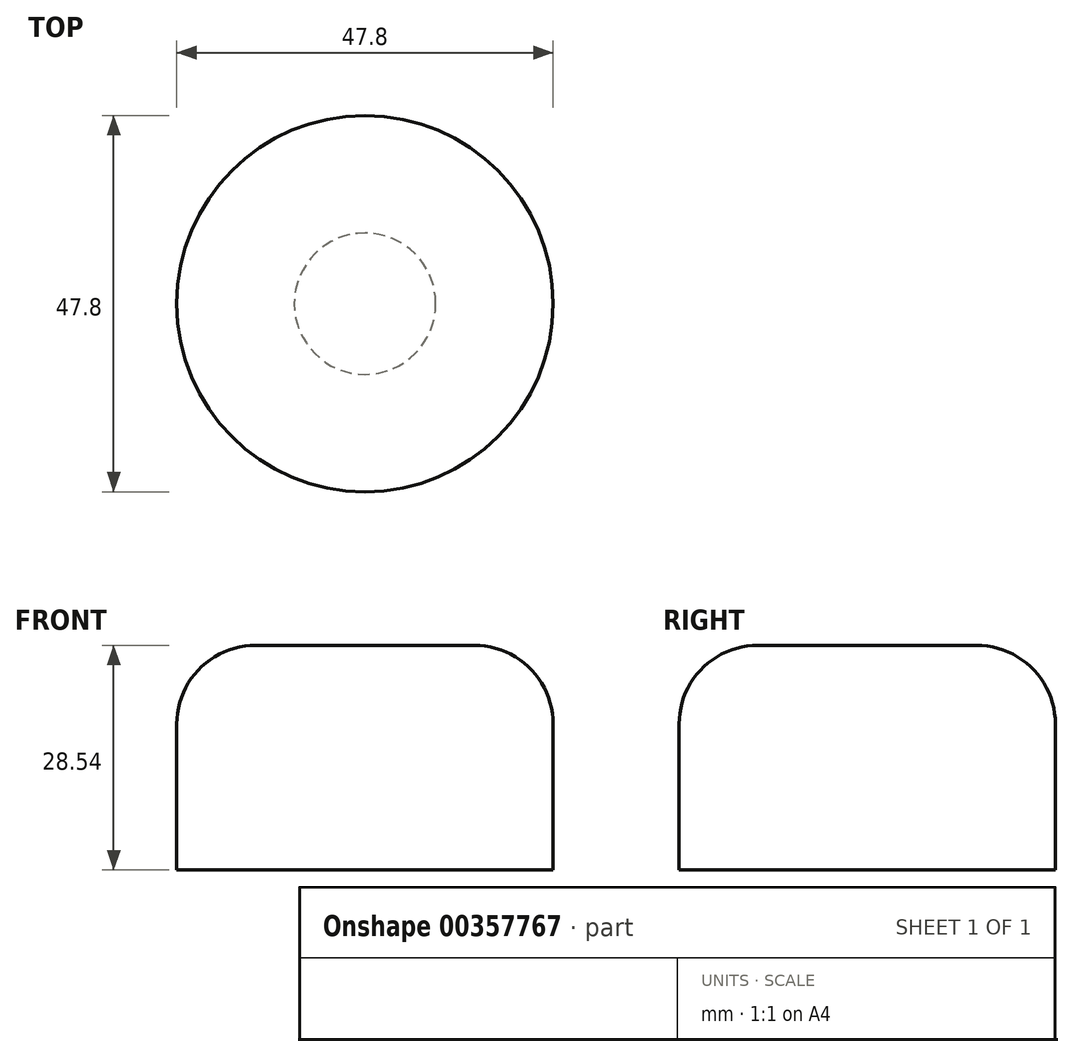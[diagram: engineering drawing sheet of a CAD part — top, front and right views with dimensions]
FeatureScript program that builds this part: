
annotation { "Feature Type Name" : "Feature", "Feature Type Description" : "" }
export const myFeature = defineFeature(function(context is Context, id is Id, definition is map)
    precondition{}
    {
        {
            var Q0;
            Q0=qCreatedBy(makeId("Top.planeOp"),FACE);
            var sketch = newSketch(context, id + "F0", { "sketchPlane" : qUnion([Q0])});
            skCircle(sketch, "E0", {"center": v(0, 0) * mm, "radius": 23.9 * mm});
            skSolve(sketch);
        }
        {
            var Q0;
            Q0=makeQuery(id+"F0.imprint","IMPRINT",FACE,{"disambiguationData":[TD([[makeQuery(id+"F0.imprint","IMPRINT",EDGE,{"derivedFrom":sQuery(id+"F0.wireOp",EDGE,"E0")}),1.0]])]});
            extrude(context, id + "F1", {"entities" : qUnion([Q0]), "depth" : 28.5 * mm});
        }
        {
            var Q0;
            Q0=makeQuery(id+"F1.opExtrude","CAP_FACE",FACE,{"disambiguationData":[OSD([sQuery(id+"F0.wireOp",EDGE,"E0")])],"isStart":true});
            var sketch = newSketch(context, id + "F2", { "sketchPlane" : qUnion([Q0])});
            skCircle(sketch, "E1", {"center": v(0, 0) * mm, "radius": 8.98 * mm});
            skSolve(sketch);
        }
        {
            var Q0;
            Q0=makeQuery(id+"F2.imprint","IMPRINT",FACE,{"disambiguationData":[TD([[makeQuery(id+"F2.imprint","IMPRINT",EDGE,{"derivedFrom":sQuery(id+"F2.wireOp",EDGE,"E1")}),1.0]])]});
            extrude(context, id + "F3", {"entities" : qUnion([Q0]), "operationType" : NewBodyOperationType.ADD, "depth" : 9 / 203.2 * mm});
        }
        {
            var Q0;
            Q0=makeQuery(id+"F1.opExtrude","CAP_EDGE",EDGE,{"disambiguationData":[OSD([sQuery(id+"F0.wireOp",EDGE,"E0")])],"isStart":false});
            fillet(context, id + "F4", {"entities" : qUnion([Q0]), "radius" : 10 * mm, "tangentPropagation" : true, "allowEdgeOverflow" : false});
        }
    });
